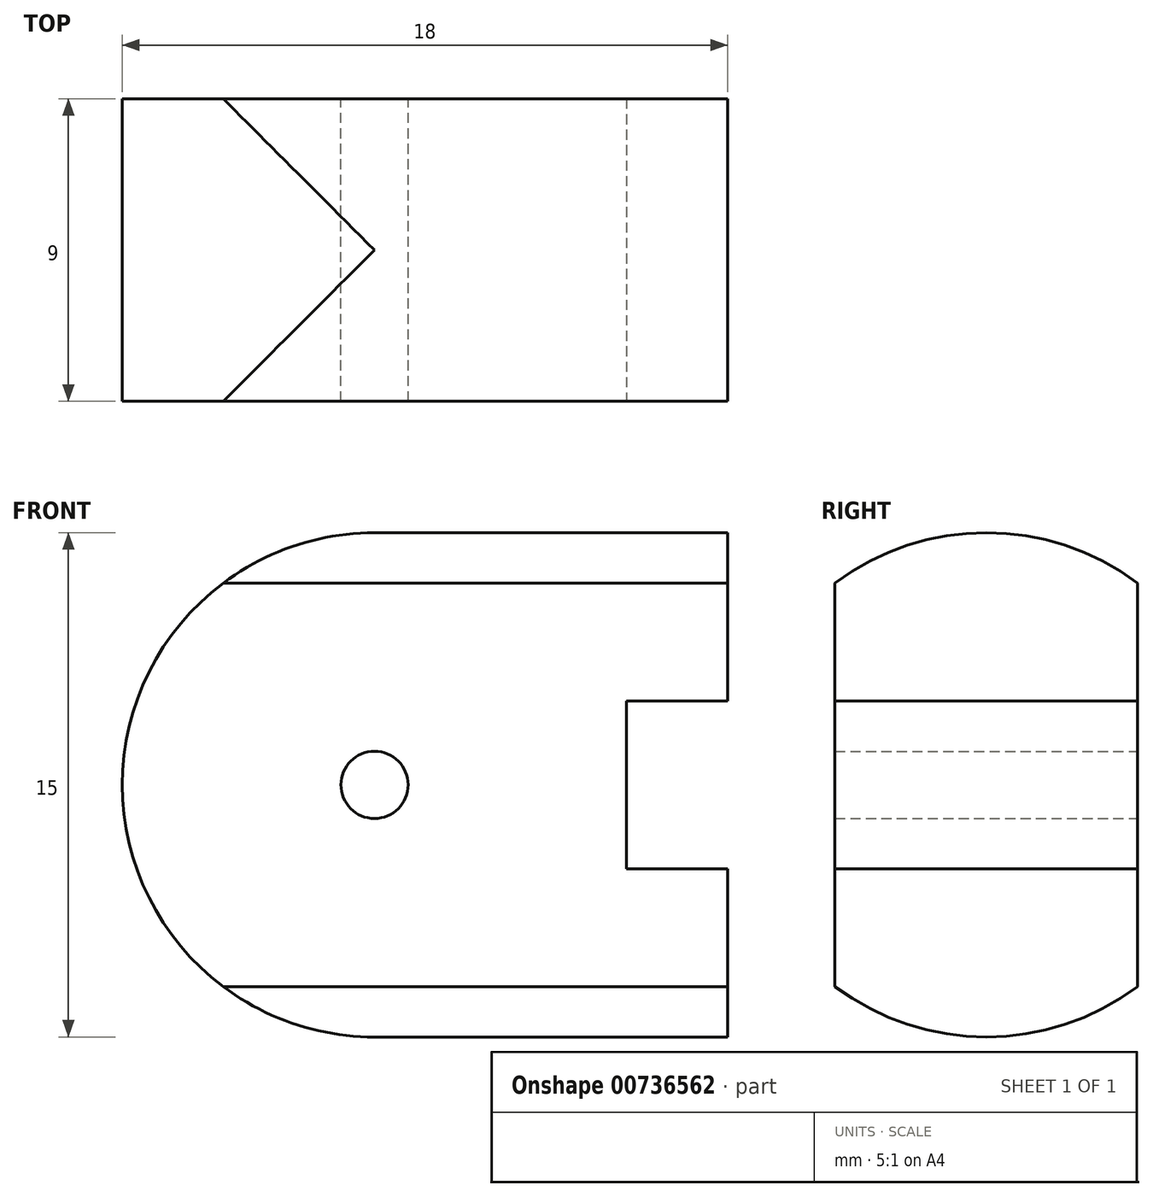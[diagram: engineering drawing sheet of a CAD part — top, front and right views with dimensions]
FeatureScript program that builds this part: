
annotation { "Feature Type Name" : "Feature", "Feature Type Description" : "" }
export const myFeature = defineFeature(function(context is Context, id is Id, definition is map)
    precondition{}
    {
        {
            var Q0;
            Q0=qCreatedBy(makeId("Front.planeOp"),FACE);
            var sketch = newSketch(context, id + "F0", { "sketchPlane" : qUnion([Q0])});
            skCircle(sketch, "E0", {"center": v(-48.89, 30.18) * mm, "radius": 7.5 * mm});
            skCircle(sketch, "E1", {"center": v(-48.89, 30.18) * mm, "radius": 1 * mm});
            skLineSegment(sketch, "E2", {"start": v(-48.89, 37.68) * mm, "end": v(-48.89, 22.68) * mm});
            skLineSegment(sketch, "E3.bottom", {"start": v(-48.89, 37.68) * mm, "end": v(-41.39, 37.68) * mm});
            skLineSegment(sketch, "E3.top", {"start": v(-48.89, 22.68) * mm, "end": v(-41.39, 22.68) * mm});
            skLineSegment(sketch, "E3.right", {"start": v(-41.39, 37.68) * mm, "end": v(-41.39, 22.68) * mm});
            skSolve(sketch);
        }
        {
            var Q0;
            {var subQ0=sQuery(id+"F0.wireOp",EDGE,"E2");var subQ1=sQuery(id+"F0.wireOp",EDGE,"E1");var subQ2=makeQuery(id+"F0.imprint","INTERSECT",VERTEX,{"disambiguationData":[OD(0.0)],"derivedFrom":[subQ1,subQ0]});Q0=makeQuery(id+"F0.imprint","IMPRINT",FACE,{"disambiguationData":[TD([[makeQuery(id+"F0.imprint","IMPRINT",EDGE,{"disambiguationData":[TD([[subQ2,1.0]])],"derivedFrom":subQ1}),-1.0]])]});}
            var Q1;
            {var subQ0=sQuery(id+"F0.wireOp",EDGE,"E2");var subQ4=sQuery(id+"F0.wireOp",EDGE,"E1");var subQ5=makeQuery(id+"F0.imprint","INTERSECT",VERTEX,{"disambiguationData":[OD(0.0)],"derivedFrom":[subQ4,subQ0]});Q1=makeQuery(id+"F0.imprint","IMPRINT",FACE,{"disambiguationData":[TD([[makeQuery(id+"F0.imprint","IMPRINT",EDGE,{"disambiguationData":[TD([[subQ5,-1.0]])],"derivedFrom":subQ4}),-1.0]])]});}
            var Q2;
            {var subQ0=sQuery(id+"F0.wireOp",EDGE,"E3.bottom");Q2=makeQuery(id+"F0.imprint","IMPRINT",FACE,{"disambiguationData":[TD([[makeQuery(id+"F0.imprint","IMPRINT",EDGE,{"derivedFrom":subQ0}),-1.0]])]});}
            var Q3;
            {var subQ0=sQuery(id+"F0.wireOp",EDGE,"E3.top");Q3=makeQuery(id+"F0.imprint","IMPRINT",FACE,{"disambiguationData":[TD([[makeQuery(id+"F0.imprint","IMPRINT",EDGE,{"derivedFrom":subQ0}),1.0]])]});}
            extrude(context, id + "F1", {"entities" : qUnion([Q0, Q1, Q2, Q3]), "depth" : 9 * mm, "offsetDistance" : 25 * mm});
        }
        {
            var Q0;
            Q0=makeQuery(id+"F1.opExtrude","SWEPT_FACE",FACE,{"disambiguationData":[OSD([sQuery(id+"F0.wireOp",EDGE,"E3.right")])]});
            var sketch = newSketch(context, id + "F2", { "sketchPlane" : qUnion([Q0])});
            skLineSegment(sketch, "E4.bottom", {"start": v(-9, 37.68) * mm, "end": v(0, 37.68) * mm});
            skLineSegment(sketch, "E4.top", {"start": v(-9, 32.68) * mm, "end": v(0, 32.68) * mm});
            skLineSegment(sketch, "E4.left", {"start": v(-9, 37.68) * mm, "end": v(-9, 32.68) * mm});
            skLineSegment(sketch, "E4.right", {"start": v(0, 37.68) * mm, "end": v(0, 32.68) * mm});
            skLineSegment(sketch, "E5.bottom", {"start": v(0, 22.68) * mm, "end": v(-9, 22.68) * mm});
            skLineSegment(sketch, "E5.top", {"start": v(0, 27.68) * mm, "end": v(-9, 27.68) * mm});
            skLineSegment(sketch, "E5.left", {"start": v(0, 22.68) * mm, "end": v(0, 27.68) * mm});
            skLineSegment(sketch, "E5.right", {"start": v(-9, 22.68) * mm, "end": v(-9, 27.68) * mm});
            skSolve(sketch);
        }
        {
            var Q0;
            Q0=makeQuery(id+"F2.imprint","IMPRINT",FACE,{"disambiguationData":[TD([[makeQuery(id+"F2.imprint","IMPRINT",EDGE,{"derivedFrom":sQuery(id+"F2.wireOp",EDGE,"E4.bottom")}),-1.0]])]});
            var Q1;
            Q1=makeQuery(id+"F2.imprint","IMPRINT",FACE,{"disambiguationData":[TD([[makeQuery(id+"F2.imprint","IMPRINT",EDGE,{"derivedFrom":sQuery(id+"F2.wireOp",EDGE,"E5.bottom")}),1.0]])]});
            extrude(context, id + "F3", {"entities" : qUnion([Q0, Q1]), "operationType" : NewBodyOperationType.ADD, "depth" : 3 * mm, "offsetDistance" : 25 * mm});
        }
        {
            var Q0;
            Q0=makeQuery(id+"F3.opExtrude","CAP_FACE",FACE,{"disambiguationData":[OSD([sQuery(id+"F2.wireOp",EDGE,"E4.bottom"),sQuery(id+"F2.wireOp",EDGE,"E4.top"),sQuery(id+"F2.wireOp",EDGE,"E4.left"),sQuery(id+"F2.wireOp",EDGE,"E4.right")])],"isStart":false});
            var sketch = newSketch(context, id + "F4", { "sketchPlane" : qUnion([Q0])});
            skCircle(sketch, "E6", {"center": v(-4.5, 30.18) * mm, "radius": 7.5 * mm});
            skLineSegment(sketch, "E7.bottom", {"start": v(-12.8, 26.8) * mm, "end": v(5.87, 26.8) * mm});
            skLineSegment(sketch, "E7.top", {"start": v(-12.8, 21.16) * mm, "end": v(5.87, 21.16) * mm});
            skLineSegment(sketch, "E7.left", {"start": v(-12.8, 26.8) * mm, "end": v(-12.8, 21.16) * mm});
            skLineSegment(sketch, "E7.right", {"start": v(5.87, 26.8) * mm, "end": v(5.87, 21.16) * mm});
            skSolve(sketch);
        }
        {
            var Q0;
            Q0=makeQuery(id+"F4.imprint","IMPRINT",FACE,{"disambiguationData":[TD([[makeQuery(id+"F4.imprint","IMPRINT",EDGE,{"derivedFrom":sQuery(id+"F4.wireOp",EDGE,"E7.top")}),1.0]])]});
            var Q1;
            {var subQ0=sQuery(id+"F4.wireOp",EDGE,"E6");var subQ1=makeQuery(id+"F3.opExtrude","CAP_EDGE",EDGE,{"disambiguationData":[OSD([sQuery(id+"F2.wireOp",EDGE,"E4.bottom")])],"isStart":false});var subQ2=makeQuery(id+"F4.imprint","INTERSECT",VERTEX,{"derivedFrom":[subQ1,subQ0]});Q1=makeQuery(id+"F4.imprint","IMPRINT",FACE,{"disambiguationData":[TD([[makeQuery(id+"F4.imprint","IMPRINT",EDGE,{"disambiguationData":[TD([[subQ2,-1.0]])],"derivedFrom":subQ0}),-1.0]])]});}
            var Q2;
            {var subQ0=sQuery(id+"F4.wireOp",EDGE,"E6");var subQ1=makeQuery(id+"F3.opExtrude","CAP_EDGE",EDGE,{"disambiguationData":[OSD([sQuery(id+"F2.wireOp",EDGE,"E4.bottom")])],"isStart":false});var subQ2=makeQuery(id+"F4.imprint","INTERSECT",VERTEX,{"derivedFrom":[subQ1,subQ0]});Q2=makeQuery(id+"F4.imprint","IMPRINT",FACE,{"disambiguationData":[TD([[makeQuery(id+"F4.imprint","IMPRINT",EDGE,{"disambiguationData":[TD([[subQ2,1.0]])],"derivedFrom":subQ0}),-1.0]])]});}
            extrude(context, id + "F5", {"entities" : qUnion([Q0, Q1, Q2]), "operationType" : NewBodyOperationType.REMOVE, "oppositeDirection" : true, "depth" : 25 * mm, "offsetDistance" : 25 * mm});
        }
    });
